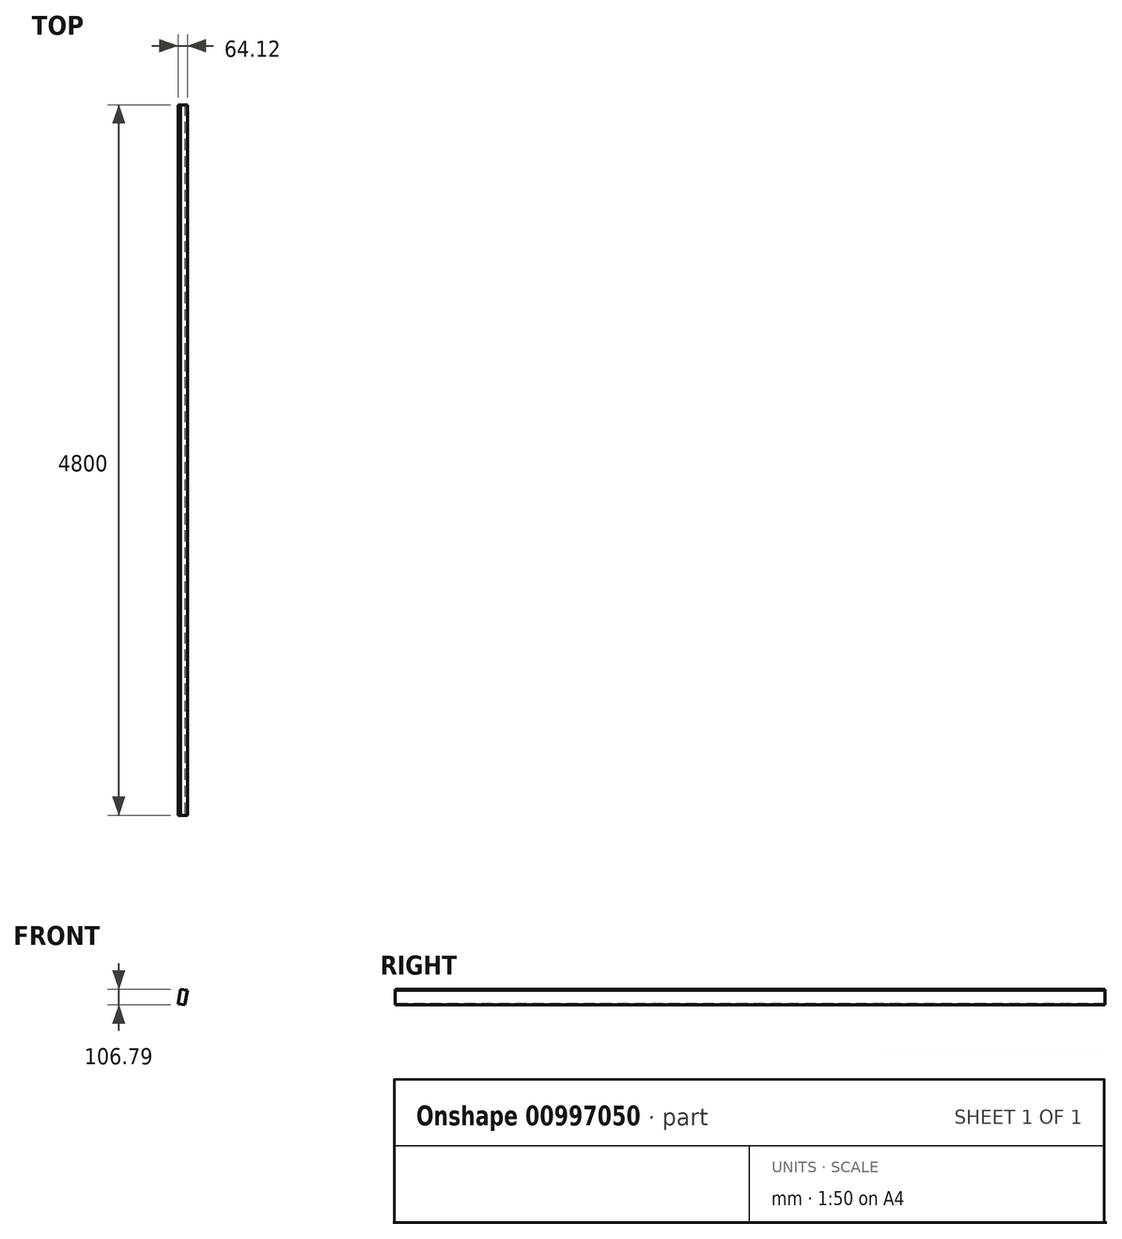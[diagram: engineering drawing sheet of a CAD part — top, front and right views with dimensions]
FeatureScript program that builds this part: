
annotation { "Feature Type Name" : "Feature", "Feature Type Description" : "" }
export const myFeature = defineFeature(function(context is Context, id is Id, definition is map)
    precondition{}
    {
        {
            var Q0;
            Q0=qCreatedBy(makeId("Front.planeOp"),FACE);
            var sketch = newSketch(context, id + "F0", { "sketchPlane" : qUnion([Q0])});
            skLineSegment(sketch, "E0.bottom", {"start": v(-60, 100) * mm, "end": v(-13, 100) * mm});
            skLineSegment(sketch, "E0.top", {"start": v(-60, 0) * mm, "end": v(-13, 0) * mm});
            skLineSegment(sketch, "E0.left", {"start": v(-60, 100) * mm, "end": v(-60, 0) * mm});
            skLineSegment(sketch, "E0.right", {"start": v(-13, 100) * mm, "end": v(-13, 0) * mm});
            skSolve(sketch);
        }
        {
            var Q0;
            Q0=makeQuery(id+"F0.imprint","IMPRINT",FACE,{"disambiguationData":[TD([[makeQuery(id+"F0.imprint","IMPRINT",EDGE,{"derivedFrom":sQuery(id+"F0.wireOp",EDGE,"E0.bottom")}),-1.0]])]});
            extrude(context, id + "F1", {"entities" : qUnion([Q0]), "oppositeDirection" : true, "depth" : 4800 * mm, "offsetDistance" : 25 * mm});
        }
        {
            var Q0;
            Q0=makeQuery(id+"F1.opExtrude","SWEPT_BODY",BODY,{"disambiguationData":[OSD([sQuery(id+"F0.wireOp",EDGE,"E0.bottom"),sQuery(id+"F0.wireOp",EDGE,"E0.top"),sQuery(id+"F0.wireOp",EDGE,"E0.left"),sQuery(id+"F0.wireOp",EDGE,"E0.right")])]});
            var Q1;
            Q1=makeQuery(id+"F1.opExtrude","SWEPT_EDGE",EDGE,{"disambiguationData":[OSD([sQuery(id+"F0.wireOp",EDGE,"E0.top"),sQuery(id+"F0.wireOp",EDGE,"E0.right")])]});
            transform(context, id + "F2", {"entities" : qUnion([Q0]), "transformType" : TransformType.ROTATION, "transformAxis" : qUnion([Q1]), "angle" : 169.7 * degree, "makeCopy" : false});
        }
    });
